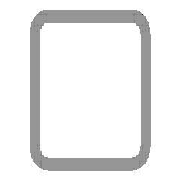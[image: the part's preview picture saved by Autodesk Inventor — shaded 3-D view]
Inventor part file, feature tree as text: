
AUTODESK INVENTOR PART (.ipt)
format: ipt  version: 2022 (Build 260153000, 153)  size: 139,264 bytes
history: native  units: mm (DEFAULTED — no unit token found)
features: other x4, plane x3, sketch x3, split x2
ambient origin geometry x8: Origin, YZ Plane, XZ Plane, XY Plane, X Axis, Y Axis, Z Axis, Center Point
bodies: Solid1 (feature_tree), Body (feature_tree)
feature tree (12):
  parser-record x1  (decoder bookkeeping rows leaked as tree rows — omitted from the tree; the rows remain in map.json)
  other  "Driven Length"
  other  "Start Plane"
  other  "End Plane"
  plane  "Work Plane4"
  split  "Split1"
  plane  "Work Plane5"
  split  "Split2"
  sketch  "Sketch"  dims[d7=8.0mm d9=40.0mm d11=40.0mm d12=4.0mm d13=20.0mm d14=220.0mm d15=20.0mm d16=20.0mm d17=90.0deg d18=200.0mm]
  sketch  "Sketch3"  dims[d3=200.0mm]
  plane  "Work Plane3"
  sketch  "Sketch4"  dims[d4=0.0mm]
